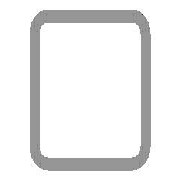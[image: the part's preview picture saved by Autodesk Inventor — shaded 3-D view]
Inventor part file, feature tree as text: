
AUTODESK INVENTOR PART (.ipt)
format: ipt  version: 2024 (Build 280153000, 153)  size: 137,216 bytes
history: native  units: mm (DEFAULTED — no unit token found)
features: other x4, plane x3, split x2, extrude x1, sketch x1
ambient origin geometry x8: Origin, YZ Plane, XZ Plane, XY Plane, X Axis, Y Axis, Z Axis, Center Point
bodies: Solid1 (feature_tree)
feature tree (11):
  parser-record x1  (decoder bookkeeping rows leaked as tree rows — omitted from the tree; the rows remain in map.json)
  other  "Driven Length"
  other  "Plano inicial"
  other  "Plano final"
  extrude  "Cuerpo"  TaperAngle=0.0deg  [1 undecoded]
  plane  "Plano de trabajo4"
  split  "Dividir1"
  plane  "Plano de trabajo5"
  split  "Dividir2"
  sketch  "Sketch3"  dims[d3=2149.2mm d4=0.0mm d10=50.8mm d11=50.8mm d12=3.175mm d13=25.4mm d14=2174.6mm d15=25.4mm d16=25.4mm d17=6.35mm d18=90.0deg d19=2149.2mm]
  plane  "Work Plane3"
note: 1 required parameter value undecoded (feature->parameter linkage not recoverable at this tier; creation-order binding heuristic only, values carry confidence <= 0.55)
